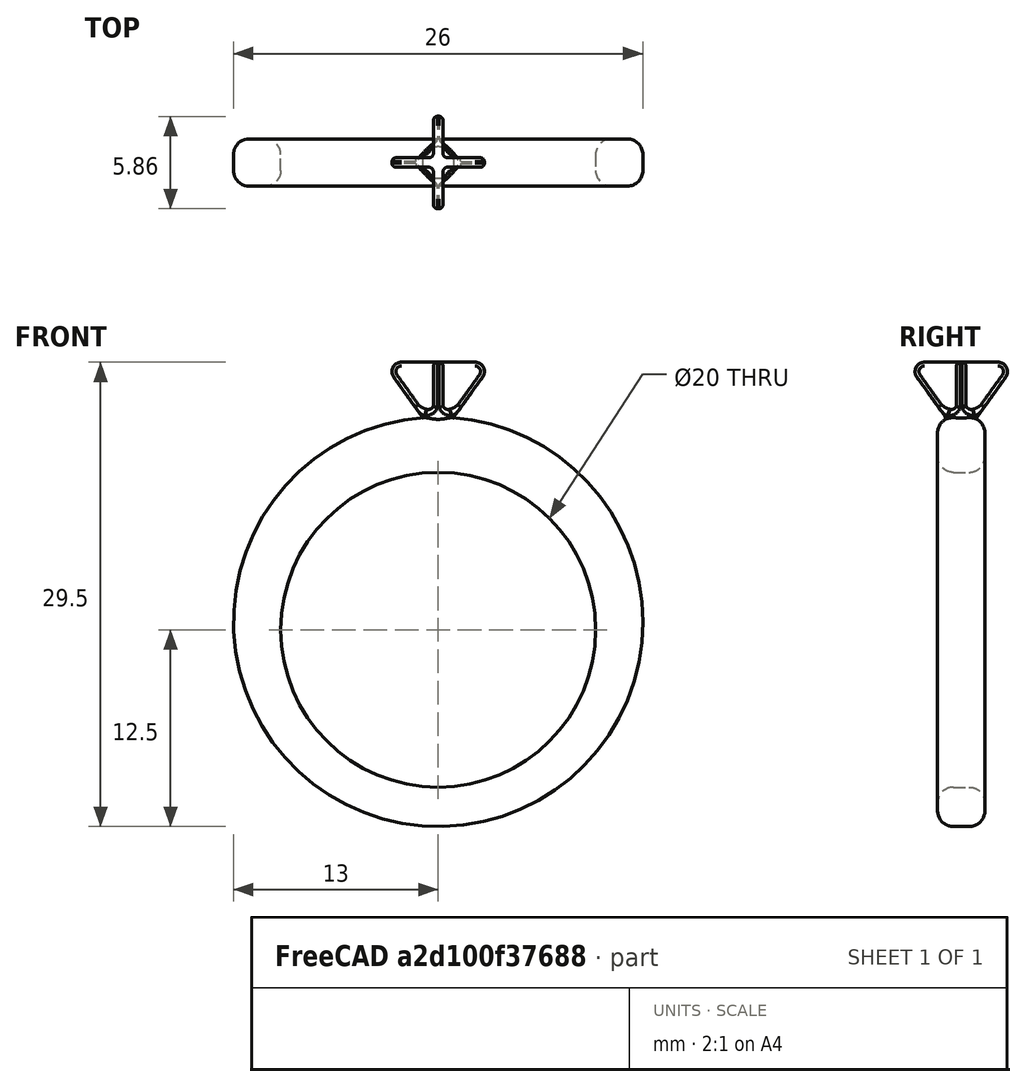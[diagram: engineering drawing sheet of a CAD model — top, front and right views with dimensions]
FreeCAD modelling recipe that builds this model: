
FCSTD DOCUMENT  (FreeCAD 0.21R33771 (Git))
Label: Anillo_freeCAD
License: All rights reserved
LicenseURL: https://en.wikipedia.org/wiki/All_rights_reserved
objects: Part::Feature×14, Part::Cut×5, Part::Fillet×4, Part::Cylinder×3, Part::MultiFuse×3, Part::Mirroring×3, Part::Loft×2, Part::Cone×1, Part::Box×1, Part::RegularPolygon×1, Part::Compound×1, Part::FeaturePython×1
note: 38 computed .brp shape members not serialized (recipe doc carries the construction recipe); baked Part::Feature solids carry a one-line shape summary decoded from their .brp

FEATURE [Part::Cone] Cone
  Angle = 360
  AttacherType = Attacher::AttachEngine3D
  Height = 3.5
  Radius1 = 1
  Radius2 = 3.5
FEATURE [Part::Cylinder] Cylinder
  Angle = 360
  AttacherType = Attacher::AttachEngine3D
  FirstAngle = 0
  Height = 2
  Placement = pos=(0,0,-2) rot=(0,0,1;0rad)
  Radius = 1
  SecondAngle = 0
FEATURE [Part::MultiFuse] Fusion
  Shapes = -> [Cone,Cylinder]
FEATURE [Part::Fillet] Fillet
  Base = -> Fusion
  Edges = 1 edges r=0.6: [Edge1]
FEATURE [Part::Box] Box  label="Cube"
  AttacherType = Attacher::AttachEngine3D
  Height = 10
  Length = 10
  Placement = pos=(0.3,0.3,0.5) rot=(0,0,1;0rad)
  Width = 10
FEATURE [Part::Fillet] Fillet001
  Base = -> Box
  Edges = 12 edges r=0.3: [Edge1,Edge2,Edge3,Edge4,Edge5,Edge6,Edge7,Edge8,Edge9,Edge10,Edge11,Edge12]
FEATURE [Part::Mirroring] Part__Mirroring  label="Fillet001 (Mirror #1)"
  Base = (0,0,0)
  Normal = (0,1,0)
  Source = -> Fillet001
FEATURE [Part::Mirroring] Part__Mirroring001  label="Fillet001 (Mirror #2)"
  Base = (0,0,0)
  Normal = (1,0,0)
  Source = -> Part__Mirroring
FEATURE [Part::Mirroring] Part__Mirroring002  label="Fillet001 (Mirror #3)"
  Base = (0,0,0)
  Normal = (1,0,0)
  Source = -> Fillet001
FEATURE [Part::Cut] Cut
  Base = -> Fillet
  Tool = -> Fillet001
FEATURE [Part::Cut] Cut001
  Base = -> Cut
  Tool = -> Part__Mirroring002
FEATURE [Part::Cut] Cut002
  Base = -> Cut001
  Tool = -> Part__Mirroring001
FEATURE [Part::Cut] Cut003
  Base = -> Cut002
  Tool = -> Part__Mirroring
FEATURE [Part::Fillet] Fillet002
  Base = -> Cut003
  Edges = 43 edges r=0.25: [Edge2,Edge4,Edge5,Edge6,Edge7,Edge8,Edge10,Edge11,Edge12,Edge13,Edge14,Edge16,Edge17,Edge18,Edge19,Edge20,Edge22,Edge23,Edge24,Edge25,Edge26,Edge29,Edge30,Edge32,Edge34,Edge42,Edge43,Edge45,Edge47,Edge54,Edge55,Edge58,Edge60,Edge68,Edge69,Edge71,Edge73,Edge80,Edge81,Edge84,Edge85,Edge86,Edge87]
  Placement = pos=(0,-1.5,0) rot=(0,0,1;0rad)
FEATURE [Part::Cylinder] Cylinder001
  Angle = 360
  AttacherType = Attacher::AttachEngine3D
  FirstAngle = 0
  Height = 3
  Radius = 13
  SecondAngle = 0
FEATURE [Part::Cylinder] Cylinder002
  Angle = 360
  AttacherType = Attacher::AttachEngine3D
  FirstAngle = 0
  Height = 10
  Placement = pos=(0,-0.5,0) rot=(0,0,1;0rad)
  Radius = 10
  SecondAngle = 0
FEATURE [Part::Cut] Cut004
  Base = -> Cylinder001
  Tool = -> Cylinder002
FEATURE [Part::Fillet] Fillet003
  Base = -> Cut004
  Edges = 4 edges r=1: [Edge2,Edge3,Edge4,Edge5]
  Placement = pos=(0,-2.9e-15,-13) rot=(1,0,0;1.5708rad)
FEATURE [Part::MultiFuse] Fusion001
  Placement = pos=(0,1.5,0) rot=(0,0,1;0rad)
  Shapes = -> [Fillet002,Fillet003]
FEATURE [Part::RegularPolygon] RegularPolygon003  label="Regular polygon003"
  AttacherType = Attacher::AttachEngine3D
  Circumradius = 0.001
  Placement = pos=(0,0,-4) rot=(0,0,1;0rad)
  Polygon = 12
FEATURE [Part::Feature] Edge
  shape: bbox 0.2561 x 0.6589 x 0.375 mm, 0 faces, 0 solids (baked)
FEATURE [Part::Feature] Edge001
  shape: bbox 0.6589 x 0.2561 x 0.375 mm, 0 faces, 0 solids (baked)
FEATURE [Part::Feature] Edge002
  shape: bbox 0.7561 x 0.2071 x 0.375 mm, 0 faces, 0 solids (baked)
FEATURE [Part::Feature] Edge003
  shape: bbox 0.2071 x 0.7561 x 0.375 mm, 0 faces, 0 solids (baked)
FEATURE [Part::Feature] Edge004
  shape: bbox 0.7584 x 0.1987 x 0.375 mm, 0 faces, 0 solids (baked)
FEATURE [Part::Feature] Edge005
  shape: bbox 0.1076 x 0.6987 x 0.375 mm, 0 faces, 0 solids (baked)
FEATURE [Part::Feature] Face004
  shape: bbox 1.228 x 1.228 x 0.4125 mm, 1 faces, 0 solids (baked)
FEATURE [Part::Feature] Face005
  shape: bbox 1.134 x 1.134 x 0.4125 mm, 1 faces, 0 solids (baked)
FEATURE [Part::Feature] Face006
  shape: bbox 1.137 x 1.357 x 0.4125 mm, 1 faces, 0 solids (baked)
FEATURE [Part::Feature] Face007
  shape: bbox 1.028 x 1.294 x 0.4125 mm, 1 faces, 0 solids (baked)
FEATURE [Part::Compound] Compound001
  Links = -> [Face007,Face004,Face005,Face006]
FEATURE [Part::FeaturePython] Array  # Draft array (typed FeaturePython)
  AlwaysSyncPlacement = false
  Angle = 360
  ArrayType = 1
  Axis = (0,0,1)
  Base = -> Compound001
  Center = (0,0,0)
  Count = 12
  ExpandArray = false
  Fuse = false
  IntervalAxis = (0,0,0)
  IntervalX = (100,0,0)
  IntervalY = (0,100,0)
  IntervalZ = (0,0,100)
  NumberCircles = 3
  NumberPolar = 12
  NumberX = 1
  NumberY = 4
  NumberZ = 1
  PlacementList = 12 placements: [(0,0,0),(0,0,0),(0,0,0),(0,0,0),(0,0,0),(0,0,0),(0,0,0),(0,0,0),(0,0,0),(0,0,0),(0,0,0),(0,0,0)]
  RadialDistance = 50
  ScaleList = (12) [(1,1,1),(1,1,1),(1,1,1),(1,1,1),(1,1,1),(1,1,1),(1,1,1),(1,1,1),(1,1,1),(1,1,1),(1,1,1),(1,1,1)]
  Symmetry = 1
  TangentialDistance = 25
FEATURE [Part::Feature] Face
  shape: bbox 5.776 x 5.776 x 2e-07 mm, 1 faces, 0 solids (baked)
FEATURE [Part::Feature] Face008
  shape: bbox 4.508 x 4.508 x 2e-07 mm, 1 faces, 0 solids (baked)
FEATURE [Part::Feature] Shell
  shape: bbox 5.776 x 5.776 x 0.8 mm, 6 faces, 0 solids (baked)
FEATURE [Part::Feature] Array_solid  label="Array (Solid)"
  Placement = pos=(0,0,3.75) rot=(0,0,1;0rad)
  shape: bbox 5.059 x 5.059 x 0.8 mm, 48 faces (baked)
FEATURE [Part::Loft] Loft
  Closed = false
  MaxDegree = 5
  Ruled = false
  Solid = false
FEATURE [Part::Loft] Loft001
  Closed = false
  MaxDegree = 5
  Ruled = false
  Sections = -> [RegularPolygon003]
  Solid = false
FEATURE [Part::MultiFuse] Fusion002
  Placement = pos=(0,0,3.75) rot=(0,0,1;0rad)
  Shapes = -> [Face,Face008,Loft,Loft001]
